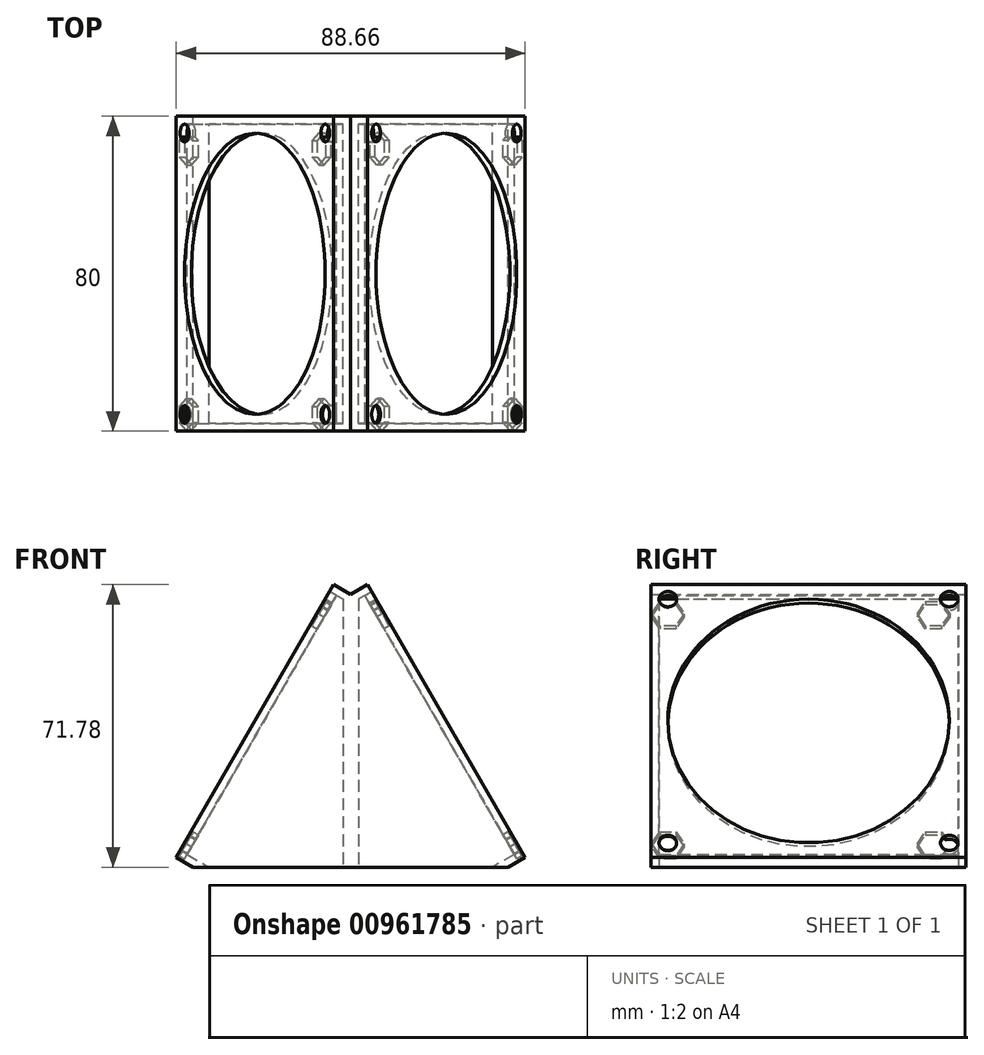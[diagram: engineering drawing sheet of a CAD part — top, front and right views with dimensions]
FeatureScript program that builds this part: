
annotation { "Feature Type Name" : "Feature", "Feature Type Description" : "" }
export const myFeature = defineFeature(function(context is Context, id is Id, definition is map)
    precondition{}
    {
        {
            var Q0;
            Q0=qCreatedBy(makeId("Front.planeOp"),FACE);
            var sketch = newSketch(context, id + "F0", { "sketchPlane" : qUnion([Q0])});
            skLineSegment(sketch, "E0", {"start": v(-40, 0) * mm, "end": v(0, 69.28) * mm});
            skLineSegment(sketch, "E1", {"start": v(0, 0) * mm, "end": v(-40, 0) * mm});
            skLineSegment(sketch, "E2", {"start": v(0, 69.28) * mm, "end": v(0, 0) * mm});
            skPoint(sketch, "E3.orphan", {"position": v(40, 0) * mm});
            skSolve(sketch);
        }
        {
            var Q0;
            Q0=makeQuery(id+"F0.imprint","IMPRINT",FACE,{"disambiguationData":[TD([[makeQuery(id+"F0.imprint","IMPRINT",EDGE,{"derivedFrom":sQuery(id+"F0.wireOp",EDGE,"E0")}),-1.0]])]});
            extrude(context, id + "F1", {"entities" : qUnion([Q0]), "endBound" : BoundingType.SYMMETRIC, "depth" : 80 * mm, "offsetDistance" : 25 * mm});
        }
        {
            var Q0;
            Q0=makeQuery(id+"F1.opExtrude","SWEPT_FACE",FACE,{"disambiguationData":[OSD([sQuery(id+"F0.wireOp",EDGE,"E0")])]});
            extrude(context, id + "F2", {"entities" : qUnion([Q0]), "operationType" : NewBodyOperationType.ADD, "depth" : 5 * mm, "offsetDistance" : 25 * mm});
        }
        {
            var Q0;
            Q0=makeQuery(id+"F2.opExtrude","CAP_FACE",FACE,{"disambiguationData":[OSD([sQuery(id+"F0.wireOp",EDGE,"E0")])],"isStart":false});
            var sketch = newSketch(context, id + "F3", { "sketchPlane" : qUnion([Q0])});
            skLineSegment(sketch, "E4.bottom", {"start": v(35.75, 55.75) * mm, "end": v(-35.75, 55.75) * mm, "construction": true});
            skLineSegment(sketch, "E4.top", {"start": v(35.75, -15.75) * mm, "end": v(-35.75, -15.75) * mm, "construction": true});
            skLineSegment(sketch, "E4.left", {"start": v(35.75, 55.75) * mm, "end": v(35.75, -15.75) * mm, "construction": true});
            skLineSegment(sketch, "E4.right", {"start": v(-35.75, 55.75) * mm, "end": v(-35.75, -15.75) * mm, "construction": true});
            skPoint(sketch, "E4.middle", {"position": v(0, 20) * mm});
            skPoint(sketch, "E4.middle.positionSnap0", {"position": v(-40, 20) * mm});
            skPoint(sketch, "E4.middle.positionSnap1", {"position": v(0, 60) * mm});
            skPoint(sketch, "E4.centerSnap0", {"position": v(-40, 20) * mm});
            skPoint(sketch, "E4.centerSnap1", {"position": v(0, 60) * mm});
            skCircle(sketch, "E5", {"center": v(0, 20) * mm, "radius": 35.75 * mm});
            skSolve(sketch);
        }
        {
            var Q0;
            Q0=makeQuery(id+"F1.opExtrude","SWEPT_FACE",FACE,{"disambiguationData":[OSD([sQuery(id+"F0.wireOp",EDGE,"E1")])]});
            shell(context, id + "F4", {"entities" : qUnion([Q0]), "thickness" : 2 * mm});
        }
        {
            var Q0;
            Q0=makeQuery(id+"F3.imprint","IMPRINT",FACE,{"disambiguationData":[TD([[makeQuery(id+"F3.imprint","IMPRINT",EDGE,{"derivedFrom":sQuery(id+"F3.wireOp",EDGE,"E5")}),1.0]])]});
            extrude(context, id + "F5", {"entities" : qUnion([Q0]), "operationType" : NewBodyOperationType.REMOVE, "oppositeDirection" : true, "depth" : 5 * mm, "offsetDistance" : 25 * mm});
        }
        {
            var Q0;
            Q0=sQuery(id+"F3.wireOp",VERTEX,"E4.bottom.start");
            var Q1;
            Q1=sQuery(id+"F3.wireOp",VERTEX,"E4.left.end");
            var Q2;
            Q2=sQuery(id+"F3.wireOp",VERTEX,"E4.right.end");
            var Q3;
            Q3=sQuery(id+"F3.wireOp",VERTEX,"E4.right.start");
            var Q4;
            Q4=makeQuery(id+"F1.opExtrude","SWEPT_BODY",BODY,{"disambiguationData":[OSD([sQuery(id+"F0.wireOp",EDGE,"E0"),sQuery(id+"F0.wireOp",EDGE,"E1"),sQuery(id+"F0.wireOp",EDGE,"E2")])]});
            hole(context, id + "F6", {"style" : HoleStyle.SIMPLE, "endStyle" : HoleEndStyle.BLIND, "holeDiameter" : 4.5 * mm, "majorDiameter" : 5 * mm, "holeDepth" : 2 * mm, "isTappedThrough" : true, "tappedDepth" : 12 * mm, "tapClearance" : 3, "locations" : qUnion([Q0, Q1, Q2, Q3]), "scope" : qUnion([Q4])});
        }
        {
            var Q0;
            Q0=makeQuery(id+"F4.opShell","OFFSET_FACE",FACE,{"disambiguationData":[OSD([sQuery(id+"F0.wireOp",EDGE,"E0")])]});
            var sketch = newSketch(context, id + "F7", { "sketchPlane" : qUnion([Q0])});
            skCircle(sketch, "E6.cCircle", {"center": v(-35.75, -15.75) * mm, "radius": 3.55 * mm, "construction": true});
            skLineSegment(sketch, "E6.0", {"start": v(-37.8, -12.2) * mm, "end": v(-33.7, -12.2) * mm});
            skLineSegment(sketch, "E6.1", {"start": v(-33.7, -12.2) * mm, "end": v(-31.65, -15.75) * mm});
            skLineSegment(sketch, "E6.2", {"start": v(-31.65, -15.75) * mm, "end": v(-33.7, -19.3) * mm});
            skLineSegment(sketch, "E6.3", {"start": v(-33.7, -19.3) * mm, "end": v(-37.8, -19.3) * mm});
            skLineSegment(sketch, "E6.4", {"start": v(-37.8, -19.3) * mm, "end": v(-39.85, -15.75) * mm});
            skLineSegment(sketch, "E6.5", {"start": v(-39.85, -15.75) * mm, "end": v(-37.8, -12.2) * mm});
            skPoint(sketch, "E6.0.midPoint", {"position": v(-35.75, -12.2) * mm});
            skLineSegment(sketch, "E7.0.1.0", {"start": v(-39.85, 51.75) * mm, "end": v(-37.8, 55.3) * mm});
            skLineSegment(sketch, "E7.0.1.1", {"start": v(-37.8, 55.3) * mm, "end": v(-33.7, 55.3) * mm});
            skLineSegment(sketch, "E7.0.1.2", {"start": v(-33.7, 55.3) * mm, "end": v(-31.65, 51.75) * mm});
            skLineSegment(sketch, "E7.0.1.3", {"start": v(-31.65, 51.75) * mm, "end": v(-33.7, 48.2) * mm});
            skLineSegment(sketch, "E7.0.1.4", {"start": v(-37.8, 48.2) * mm, "end": v(-39.85, 51.75) * mm});
            skLineSegment(sketch, "E7.0.1.5", {"start": v(-33.7, 48.2) * mm, "end": v(-37.8, 48.2) * mm});
            skLineSegment(sketch, "E7.1.0.0", {"start": v(27.65, -15.75) * mm, "end": v(29.7, -12.2) * mm});
            skLineSegment(sketch, "E7.1.0.1", {"start": v(29.7, -12.2) * mm, "end": v(33.8, -12.2) * mm});
            skLineSegment(sketch, "E7.1.0.2", {"start": v(33.8, -12.2) * mm, "end": v(35.85, -15.75) * mm});
            skLineSegment(sketch, "E7.1.0.3", {"start": v(35.85, -15.75) * mm, "end": v(33.8, -19.3) * mm});
            skLineSegment(sketch, "E7.1.0.4", {"start": v(29.7, -19.3) * mm, "end": v(27.65, -15.75) * mm});
            skLineSegment(sketch, "E7.1.0.5", {"start": v(33.8, -19.3) * mm, "end": v(29.7, -19.3) * mm});
            skLineSegment(sketch, "E7.1.1.0", {"start": v(27.65, 51.75) * mm, "end": v(29.7, 55.3) * mm});
            skLineSegment(sketch, "E7.1.1.1", {"start": v(29.7, 55.3) * mm, "end": v(33.8, 55.3) * mm});
            skLineSegment(sketch, "E7.1.1.2", {"start": v(33.8, 55.3) * mm, "end": v(35.85, 51.75) * mm});
            skLineSegment(sketch, "E7.1.1.3", {"start": v(35.85, 51.75) * mm, "end": v(33.8, 48.2) * mm});
            skLineSegment(sketch, "E7.1.1.4", {"start": v(29.7, 48.2) * mm, "end": v(27.65, 51.75) * mm});
            skLineSegment(sketch, "E7.1.1.5", {"start": v(33.8, 48.2) * mm, "end": v(29.7, 48.2) * mm});
            skLineSegment(sketch, "E7.direction1", {"start": v(-39.85, -15.75) * mm, "end": v(27.65, -15.75) * mm, "construction": true});
            skLineSegment(sketch, "E7.direction2", {"start": v(-39.85, -15.75) * mm, "end": v(-39.85, 51.75) * mm, "construction": true});
            skSolve(sketch);
        }
        {
            var Q0;
            Q0 = qSketchRegion(id + "F7", true);
            extrude(context, id + "F8", {"entities" : qUnion([Q0]), "operationType" : NewBodyOperationType.REMOVE, "oppositeDirection" : true, "depth" : 1.5 * mm, "offsetDistance" : 25 * mm});
        }
        {
            var Q0;
            Q0=makeQuery(id+"F1.opExtrude","SWEPT_BODY",BODY,{"disambiguationData":[OSD([sQuery(id+"F0.wireOp",EDGE,"E0"),sQuery(id+"F0.wireOp",EDGE,"E1"),sQuery(id+"F0.wireOp",EDGE,"E2")])]});
            var Q1;
            Q1=makeQuery(id+"F1.opExtrude","SWEPT_FACE",FACE,{"disambiguationData":[OSD([sQuery(id+"F0.wireOp",EDGE,"E2")])]});
            mirror(context, id + "F9", {"operationType" : NewBodyOperationType.ADD, "entities" : qUnion([Q0]), "mirrorPlane" : qUnion([Q1])});
        }
    });
